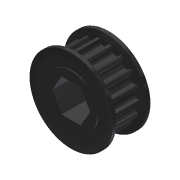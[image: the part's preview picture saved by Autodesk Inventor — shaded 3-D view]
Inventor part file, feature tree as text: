
AUTODESK INVENTOR PART (.ipt)
format: ipt  version: 2013 (Build 170138000, 138)  size: 523,264 bytes
history: native  units: in
note: dims shown in document units (in); Inventor stores cm internally (conversion verified against a paired STEP export)
features: mirror x1, other x1, imported_body x1
ambient origin geometry x8: Origin, YZ Plane, XZ Plane, XY Plane, X Axis, Y Axis, Z Axis, Center Point
feature tree (3):
  mirror  "Mirror1"
  other  "217-3225-STEP1"
  imported_body  "Base1"
